# Revit family: IS_Ceraplus_A6152_BIM_DE
name_source: partatom
category: Plumbing Fixtures
revit_build: Autodesk Revit MEP 2016 (Build: 20161004_0715(x64)
units: mm (PartAtom-declared; Revit-internal decimal feet)

## family parameters
Always vertical = No
Cut with Voids When Loaded = No
OmniClass Number = 23.45.55.17
OmniClass Title = Mixing Faucets
Part Type = Normal
Room Calculation Point = No
Round Connector Dimension = Use Diameter
Shared = No
Work Plane-Based = No

## types (1)
- A6152AA - CERAPLUS LAV THERM EL BOCCA230 KIT2 TRAS
    Accessories = www.idealstandard.de\ersatzteile
    AreaUnits = millimeters
    Assembly Code = C1030200
    AssetType = Fixed
    BIMObjectName = ISI_IdealStandard_MixerTaps_CERAPLUS_A6152AA
    BIMobject category = Taps & Mixers
    BOSUseNativeGeometries = 1
    BarCode = 4015413332682
    Brand url = http://www.idealstandard.co.uk
    CodePerformance = DIN 4109, Gruppe 1
    Color = Chrome
    ConnectionType = Plumbing
    Cost = 0 $
    CurrencyUnit = €
    Date of publishing = 6/23/2017
    Description = CERAPLUS LAV THERM EL BOCCA230 KIT2 TRAS
    DurationUnit = year
    EAN code = https://4015413332682
    Edition number = 1
    ExpectedLife = 25
    Features = CERAPLUS build-in sensor shower mounted spout
    Finish = Chrome
    GrossWeight = 2,98 kg
    IFC Classification = Sanitary Terminal
    Installation instructions = http://www.idealstandard.de
    InstallationDate = 1900-12-31T23:59:59
    InstallationInstructions = www.idealstandard.de\produkte
    LinearUnits = millimeters
    Manufacturer name = Ideal Standard
    ManufacturerURL = www.idealstandard.de
    Material = Brass
    Material main = Brass
    Model = A6152AA
    ModelNumber = A6152AA
    ModelReference = IS Sensor-Wand-WT-Arm.UP CERAPLUS, BS2, Temp.über Griff,Netz., Ausl.230mm, Chrom
    NBS Reference Code = 35-06-07
    NBS Reference Description = Bath Water Supply Fittings
    Name = ISI_IdealStandard_MixerTaps_CERAPLUS_A6152AA
    Nominal height = 0
    Nominal width = 0
    NominalDepth = 0 mm  [stored 0 ft]
    NominalLength = 240 mm
    OmniClass Code = 23-31 11 00
    OmniClass Description = Faucets
    Product Guid = 8339f61c-e4ef-40a6-a666-ae2a05e96fd4
    Product SKU = A6152
    Product data url = https://bimobject.com
    Product family = CERAPLUS
    Product group = Basin Mixer
    Product url = http://www.idealstandard.de
    ProductInformation = www.idealstandard.de
    QR code = http://bimobject.com
    Shape = Sculptured
    Size = 170 x 170 x 240 mm
    Space = Internal
    Technical description = http://www.idealstandard.de
    URL = www.idealstandard.de
    Uniclass 1.4 Code = L8212
    Uniclass 1.4 Description = Fittings
    Uniclass 2.0 Code = PR-35-06-07
    Uniclass 2.0 Description = Bath Water Supply Fittings
    Uniclass 2015 Code = Pr_40_20_87_10
    Uniclass 2015 Name = Bath thermostatic water supply sets
    Uniclass2015Code = Pr_40_20_87_98
    Uniclass2015Title = Washbasin taps
    Uniclass2015Version = Products v1.1
    Version = 1
    VolumeUnits = Litres
    Weight Net (Kg) = 2.45

note: [stored X ft] marks values corroborated as IEEE doubles in the binary element streams (Revit-internal decimal feet)

## geometry (parser evidence)
native form markers: Blend x2, Sweep x3
no freeform markers — native parametric forms only
